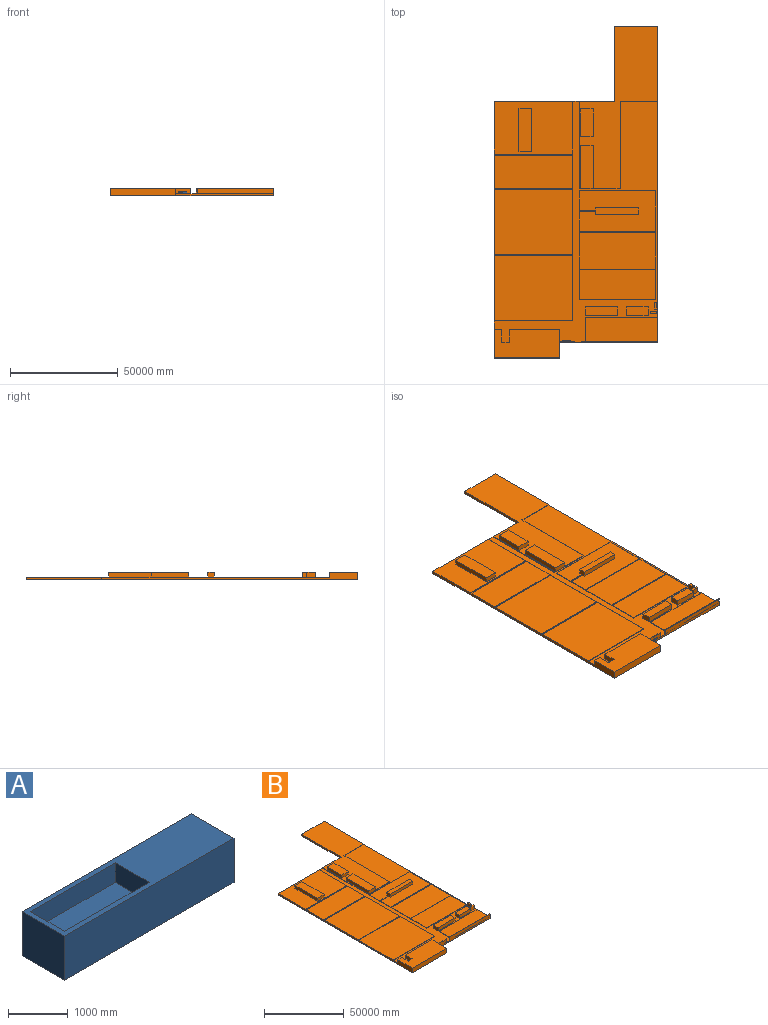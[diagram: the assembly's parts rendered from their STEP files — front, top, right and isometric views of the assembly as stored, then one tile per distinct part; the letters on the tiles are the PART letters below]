
ASSEMBLY  parts=2 mates=1
PART A: 11 faces, bbox 4000x1000x900 mm
  f0: plane 4000x1000mm, normal (0,0,1), area 2400000mm2, adj f1,f2,f3,f4,f6,f7,f8,f9
  f1: plane 4000x900mm, normal (0,1,0), area 3600000mm2, adj f0,f2,f4,f5
  f2: plane 1000x900mm, normal (-1,0,0), area 900000mm2, adj f0,f1,f3,f5
  f3: plane 4000x900mm, normal (0,-1,0), area 3600000mm2, adj f0,f2,f4,f5
  f4: plane 1000x900mm, normal (1,0,0), area 900000mm2, adj f0,f1,f3,f5
  f5: plane 4000x1000mm, normal (0,0,-1), area 4000000mm2, adj f1,f2,f3,f4
  f6: plane 2000x400mm, normal (0,-1,0), area 800000mm2, adj f0,f7,f9,f10
  f7: plane 800x400mm, normal (1,0,0), area 320000mm2, adj f0,f6,f8,f10
  f8: plane 2000x400mm, normal (0,1,0), area 800000mm2, adj f0,f7,f9,f10
  f9: plane 800x400mm, normal (-1,0,0), area 320000mm2, adj f0,f6,f8,f10
  f10: plane 2000x800mm, normal (0,0,1), area 1600000mm2, adj f6,f7,f8,f9
PART B: 102 faces, bbox 76000x154250x3500 mm
  f0: plane 112000x76000mm, normal (0,0,1), area 1647500000mm2, adj f1,f2,f5,f6,f9,f11,f12,f13
  f1: plane 35500x2500mm, normal (0,1,0), area 80375000mm2, adj f0,f2,f50,f51,f78,f79
  f2: plane 147000x3500mm, normal (1,0,0), area 159187500mm2, adj f0,f1,f3,f9,f10,f51,f69,f71
  f3: plane 20000x1250mm, normal (0,1,0), area 25000000mm2, adj f2,f4,f10,f71
  f4: plane 35000x1250mm, normal (-1,0,0), area 43750000mm2, adj f3,f5,f10,f71
  f5: plane 56000x1250mm, normal (0,1,0), area 69250000mm2, adj f0,f4,f6,f10,f52,f53,f70,f71
  f6: plane 119250x3500mm, normal (-1,0,0), area 177500000mm2, adj f0,f5,f7,f10,f18,f19,f52,f54
  f7: plane 30500x3500mm, normal (0,-1,0), area 106750000mm2, adj f6,f8,f10,f19
  f8: plane 7250x3500mm, normal (1,0,0), area 25375000mm2, adj f7,f9,f10,f19
  f9: plane 45500x3500mm, normal (0,-1,0), area 151750000mm2, adj f0,f2,f8,f10,f11,f19,f50,f51
  f10: plane 154250x76000mm, normal (0,0,-1), area 9433125000mm2, adj f2,f3,f4,f5,f6,f7,f8,f9
  f11: plane 2500x250mm, normal (1,0,0), area 625000mm2, adj f0,f9,f12,f19
  f12: plane 7000x2500mm, normal (0,1,0), area 17500000mm2, adj f0,f11,f13,f19
  f13: plane 5750x2500mm, normal (1,0,0), area 14375000mm2, adj f0,f12,f14,f19
  f14: plane 23500x2500mm, normal (0,1,0), area 58750000mm2, adj f0,f13,f15,f19
  f15: plane 6000x2500mm, normal (-1,0,0), area 15000000mm2, adj f0,f14,f16,f19
  f16: plane 3500x2500mm, normal (0,1,0), area 8750000mm2, adj f0,f15,f17,f19
  f17: plane 6000x2500mm, normal (1,0,0), area 15000000mm2, adj f0,f16,f18,f19
  f18: plane 3500x2500mm, normal (0,1,0), area 8750000mm2, adj f0,f6,f17,f19
  f19: plane 37500x13250mm, normal (0,0,1), area 384875000mm2, adj f6,f7,f8,f9,f11,f12,f13,f14
  f20: plane 15000x2500mm, normal (0,1,0), area 37500000mm2, adj f0,f21,f23,f24
  f21: plane 4000x2500mm, normal (-1,0,0), area 10000000mm2, adj f0,f20,f22,f24
  f22: plane 15000x2500mm, normal (0,-1,0), area 37500000mm2, adj f0,f21,f23,f24
  f23: plane 4000x2500mm, normal (1,0,0), area 10000000mm2, adj f0,f20,f22,f24
  f24: plane 15000x4000mm, normal (0,0,1), area 60000000mm2, adj f20,f21,f22,f23
  f25: plane 10000x2500mm, normal (0,1,0), area 25000000mm2, adj f0,f26,f28,f29
  f26: plane 4000x2500mm, normal (-1,0,0), area 10000000mm2, adj f0,f25,f27,f29
  f27: plane 10000x2500mm, normal (0,-1,0), area 25000000mm2, adj f0,f26,f28,f29
  f28: plane 4000x2500mm, normal (1,0,0), area 10000000mm2, adj f0,f25,f27,f29
  f29: plane 10000x4000mm, normal (0,0,1), area 40000000mm2, adj f25,f26,f27,f28
  f30: plane 3000x2500mm, normal (-1,0,0), area 6875000mm2, adj f0,f31,f33,f34,f84,f85,f91
  f31: plane 20000x2250mm, normal (0,-1,0), area 45000000mm2, adj f30,f32,f34,f84
  f32: plane 3000x2250mm, normal (1,0,0), area 6750000mm2, adj f31,f33,f34,f84
  f33: plane 20000x2250mm, normal (0,1,0), area 45000000mm2, adj f30,f32,f34,f84
  f34: plane 20000x3000mm, normal (0,0,1), area 60000000mm2, adj f30,f31,f32,f33
  f35: plane 6000x2250mm, normal (0,1,0), area 13500000mm2, adj f36,f38,f39,f71
  f36: plane 20000x2250mm, normal (-1,0,0), area 45000000mm2, adj f35,f37,f39,f71
  f37: plane 19000x2500mm, normal (0,-1,0), area 18250000mm2, adj f0,f36,f38,f39,f68,f70,f71
  f38: plane 20000x2250mm, normal (1,0,0), area 45000000mm2, adj f35,f37,f39,f71
  f39: plane 20000x6000mm, normal (0,0,1), area 120000000mm2, adj f35,f36,f37,f38
  f40: plane 2500x1000mm, normal (-1,0,0), area 2500000mm2, adj f0,f41,f43,f44
  f41: plane 3000x2500mm, normal (0,-1,0), area 7500000mm2, adj f0,f40,f42,f44
  f42: plane 2500x1000mm, normal (1,0,0), area 2500000mm2, adj f0,f41,f43,f44
  f43: plane 3000x2500mm, normal (0,1,0), area 7500000mm2, adj f0,f40,f42,f44
  f44: plane 3000x1000mm, normal (0,0,1), area 3000000mm2, adj f40,f41,f42,f43
  f45: plane 3000x2500mm, normal (-1,0,0), area 7500000mm2, adj f0,f46,f48,f49
  f46: plane 2500x1000mm, normal (0,-1,0), area 2500000mm2, adj f0,f45,f47,f49
  f47: plane 3000x2500mm, normal (1,0,0), area 7500000mm2, adj f0,f46,f48,f49
  f48: plane 2500x1000mm, normal (0,1,0), area 2500000mm2, adj f0,f45,f47,f49
  f49: plane 3000x1000mm, normal (0,0,1), area 3000000mm2, adj f45,f46,f47,f48
  f50: plane 2500x250mm, normal (-1,0,0), area 625000mm2, adj f0,f1,f9,f51
  f51: plane 35500x250mm, normal (0,0,1), area 8875000mm2, adj f1,f2,f9,f50
  f52: plane 36500x24500mm, normal (0,0,1), area 774250000mm2, adj f5,f6,f53,f54,f56,f57,f58,f59
  f53: plane 24500x250mm, normal (1,0,0), area 6125000mm2, adj f0,f5,f52,f54
  f54: plane 36500x250mm, normal (0,-1,0), area 9125000mm2, adj f0,f6,f52,f53
  f55: plane 20000x6000mm, normal (0,0,1), area 120000000mm2, adj f56,f57,f58,f59
  f56: plane 6000x2250mm, normal (0,1,0), area 13500000mm2, adj f52,f55,f57,f59
  f57: plane 20000x2250mm, normal (1,0,0), area 45000000mm2, adj f52,f55,f56,f58
  f58: plane 6000x2250mm, normal (0,-1,0), area 13500000mm2, adj f52,f55,f57,f59
  f59: plane 20000x2250mm, normal (-1,0,0), area 45000000mm2, adj f52,f55,f56,f58
  f60: plane 36500x250mm, normal (0,-1,0), area 9125000mm2, adj f0,f6,f61,f63
  f61: plane 15500x250mm, normal (1,0,0), area 3875000mm2, adj f0,f60,f62,f63
  f62: plane 36500x250mm, normal (0,1,0), area 9125000mm2, adj f0,f6,f61,f63
  f63: plane 36500x15500mm, normal (0,0,1), area 565750000mm2, adj f6,f60,f61,f62
  f64: plane 36500x250mm, normal (0,-1,0), area 9125000mm2, adj f0,f6,f65,f67
  f65: plane 30250x250mm, normal (1,0,0), area 7562500mm2, adj f0,f64,f66,f67
  f66: plane 36500x250mm, normal (0,1,0), area 9125000mm2, adj f0,f6,f65,f67
  f67: plane 36500x30250mm, normal (0,0,1), area 1104125000mm2, adj f6,f64,f65,f66
  f68: plane 40500x250mm, normal (1,0,0), area 10125000mm2, adj f0,f37,f69,f71
  f69: plane 17500x250mm, normal (0,-1,0), area 4375000mm2, adj f0,f2,f68,f71
  f70: plane 40500x250mm, normal (-1,0,0), area 10125000mm2, adj f0,f5,f37,f71
  f71: plane 75500x36500mm, normal (0,0,1), area 1271500000mm2, adj f2,f3,f4,f5,f35,f36,f37,f38
  f72: plane 13000x6000mm, normal (0,0,1), area 78000000mm2, adj f73,f74,f75,f76
  f73: plane 13000x2250mm, normal (1,0,0), area 29250000mm2, adj f71,f72,f74,f76
  f74: plane 6000x2250mm, normal (0,-1,0), area 13500000mm2, adj f71,f72,f73,f75
  f75: plane 13000x2250mm, normal (-1,0,0), area 29250000mm2, adj f71,f72,f74,f76
  f76: plane 6000x2250mm, normal (0,1,0), area 13500000mm2, adj f71,f72,f73,f75
  f77: plane 33500x250mm, normal (0,1,0), area 8375000mm2, adj f0,f2,f78,f79
  f78: plane 11250x250mm, normal (-1,0,0), area 2812500mm2, adj f0,f1,f77,f79
  f79: plane 33500x11250mm, normal (0,0,1), area 376875000mm2, adj f1,f2,f77,f78
  f80: plane 36500x250mm, normal (0,-1,0), area 9125000mm2, adj f0,f6,f81,f83
  f81: plane 30250x250mm, normal (1,0,0), area 7562500mm2, adj f0,f80,f82,f83
  f82: plane 36500x250mm, normal (0,1,0), area 9125000mm2, adj f0,f6,f81,f83
  f83: plane 36500x30250mm, normal (0,0,1), area 1104125000mm2, adj f6,f80,f81,f82
  f84: plane 35500x19000mm, normal (0,0,1), area 610750000mm2, adj f30,f31,f32,f33,f85,f86,f87,f88
  f85: plane 7500x250mm, normal (0,1,0), area 1875000mm2, adj f0,f30,f84,f86
  f86: plane 9250x250mm, normal (-1,0,0), area 2312500mm2, adj f0,f84,f85,f87
  f87: plane 35500x250mm, normal (0,-1,0), area 8875000mm2, adj f0,f84,f86,f88
  f88: plane 19000x250mm, normal (1,0,0), area 4750000mm2, adj f0,f84,f87,f89
  f89: plane 35500x250mm, normal (0,1,0), area 8875000mm2, adj f0,f84,f88,f90
  f90: plane 9250x250mm, normal (-1,0,0), area 2312500mm2, adj f0,f84,f89,f91
  f91: plane 7500x250mm, normal (0,-1,0), area 1875000mm2, adj f0,f30,f84,f90
  f92: plane 17000x250mm, normal (-1,0,0), area 4250000mm2, adj f0,f93,f95,f96
  f93: plane 35500x250mm, normal (0,-1,0), area 8875000mm2, adj f0,f92,f94,f96
  f94: plane 17000x250mm, normal (1,0,0), area 4250000mm2, adj f0,f93,f95,f96
  f95: plane 35500x250mm, normal (0,1,0), area 8875000mm2, adj f0,f92,f94,f96
  f96: plane 35500x17000mm, normal (0,0,1), area 603500000mm2, adj f92,f93,f94,f95
  f97: plane 14000x250mm, normal (-1,0,0), area 3500000mm2, adj f0,f98,f100,f101
  f98: plane 35500x250mm, normal (0,-1,0), area 8875000mm2, adj f0,f97,f99,f101
  f99: plane 14000x250mm, normal (1,0,0), area 3500000mm2, adj f0,f98,f100,f101
  f100: plane 35500x250mm, normal (0,1,0), area 8875000mm2, adj f0,f97,f99,f101
  f101: plane 35500x14000mm, normal (0,0,1), area 497000000mm2, adj f97,f98,f99,f100
PLACE A t=(-5909.6,-55765.87,-2849.71)mm
PLACE B t=(-37465.13,-55757.67,-2849.71)mm
MATE planar A.f3 <-> B.f16  axis (0,-1,0) through (-3965.13,-55757.67,-2849.71)mm
